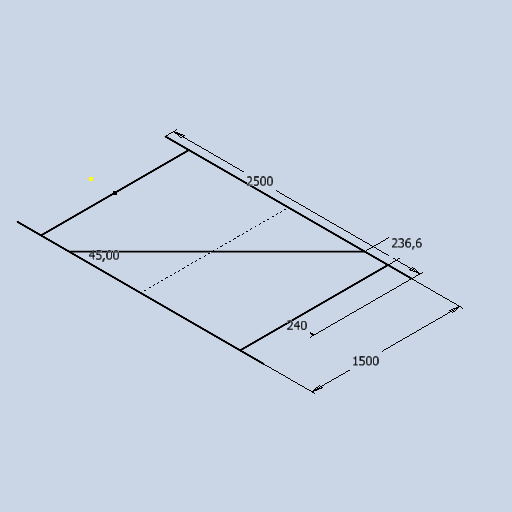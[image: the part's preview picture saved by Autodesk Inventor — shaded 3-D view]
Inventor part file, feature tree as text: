
AUTODESK INVENTOR PART (.ipt)
format: ipt  version: 2025 (Build 290162010, 162A)  size: 257,536 bytes
history: native  units: mm
features: sketch x1
ambient origin geometry x8: Origin, YZ Plane, XZ Plane, XY Plane, X Axis, Y Axis, Z Axis, Center Point
feature tree (1):
  sketch  "Sketch1"  dims[d5=2500.0mm d6=1500.0mm d7=240.0mm d8=45.0deg d9=236.6mm]
